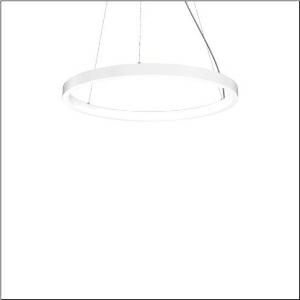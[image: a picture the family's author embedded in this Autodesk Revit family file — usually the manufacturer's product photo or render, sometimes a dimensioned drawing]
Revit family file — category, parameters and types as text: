
# Revit family: silica_r__21_ring-i_5pjbi3d1004a_d7a1
name_source: partatom
category: Lighting Fixtures
units: mm (PartAtom-declared; Revit-internal decimal feet)

## family parameters
Cut with Voids When Loaded = No
Host = Face
Light Source = No
Part Type = Normal
Room Calculation Point = No
Round Connector Dimension = Use Diameter
Shared = No

## types (1)
- Silica® 21 Ring-I (1 x LED, 6120 lm, 105 W, 3000K)
    Apparent Load = 105 VA
    CIE Flux Codes = 22 48 76 50 101
    Color Rendering = 80
    Color Temperature = 3000K
    Default Elevation = 1800 mm
    Description = Silica® 21 Ring-I, suspended luminaire, of PMMA, frosted, light emission: inner ring side luminous distribution, primary light characteristic: symmetric, installation type: suspended mounting, LED, rated luminous flux: 6.120lm, luminous efficacy: 58lm/W, light colour: 830, colour temperature: 3000K, control gear: DALI 2, with terminal, 5-pole, mains connection: 230V, AC/DC, 0/50..60Hz, rated input power: 105W, housing, of extruded aluminium section, traffic white (RAL 9016), diameter: 1.090mm, ceiling canopy, traffic white (RAL 9016), protection rating (lamp compartment): IP40, insulation class (complete): insulation class I (protective earthing), certification: CE, impact resistance: IK02, permissible operating ambient temperature: 0..+35°C, packaging unit: 1 piece
    Height = 48 mm  [stored 0.15748 ft]
    Lamp = 1 x LED
    Lamp Light Flux = 6120 lm
    Lamp Power = 105 W
    Lamp count = 1
    Length = 1090 mm
    Luminous efficacy = 58 lm/W
    Manufacturer = Siteco
    ModVariant = No
    Model = 5PJBI3D1004A
    Mounting Place = Ceiling
    Mounting Type = Pendant
    Number of Poles = 1
    OnlyDefault = Yes
    Power Factor = 1
    Product Name = Silica® 21 Ring-I
    Product group = suspended luminaire
    ProductGroupID = 904
    Protection Class = Protection class I
    Protection Degree = IP 40
    RLX_Detail_Level = 1
    RLX_Emergency_Light_Flux = 0 lm
    RLX_Emergency_Type = 0
    RLX_Emergency_Type_DB = No
    RlxData = <blob elided: 12809 chars, md5=24c3c826>
    Socket = socket
    Standby Power = 0 W
    System Light Flux = 6120 lm
    System Power = 105 W
    Type Comments = Product without accessories
    Type Image = l_1258371.jpg
    URL = http://relux.com
    VarID = ---
    Voltage = 0 V
    Weight = 0.00 kg
    Width = 0 mm  [stored 0 ft]

note: [stored X ft] marks values corroborated as IEEE doubles in the binary element streams (Revit-internal decimal feet)

## geometry (parser evidence)
native form markers: Sweep x12
no freeform markers — native parametric forms only
